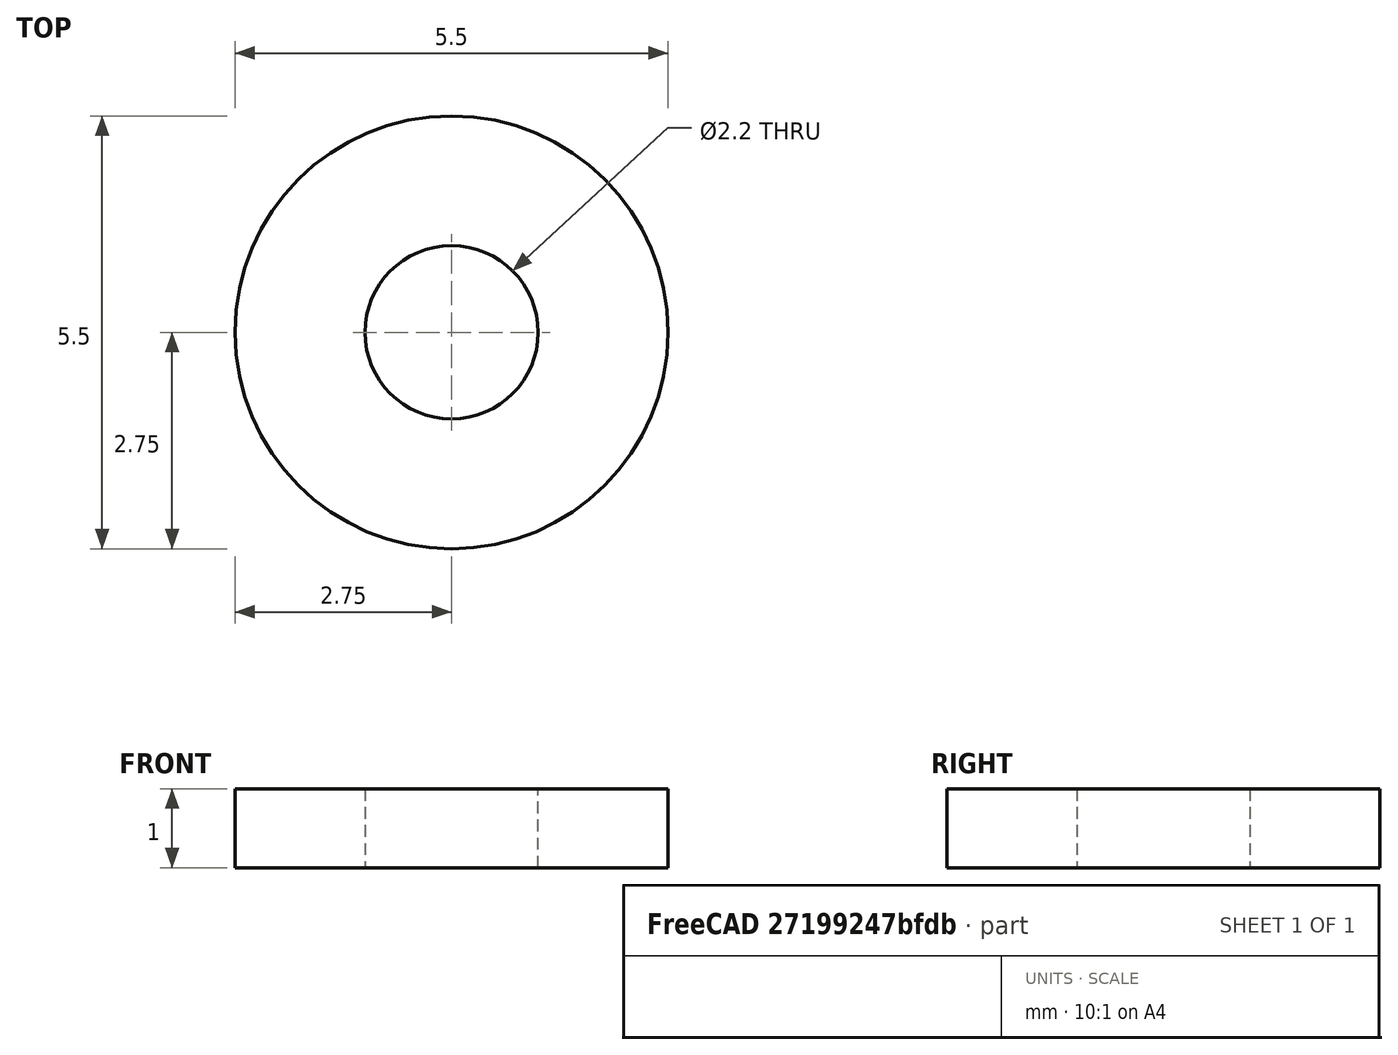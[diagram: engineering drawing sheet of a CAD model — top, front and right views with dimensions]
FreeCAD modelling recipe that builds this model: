
FCSTD DOCUMENT  (FreeCAD 0.18R13959 (Git))
Label: Washer_M2x1mm
License: CreativeCommons Attribution-NonCommercial-ShareAlike
LicenseURL: http://creativecommons.org/licenses/by-nc-sa/4.0/
objects: Sketcher::SketchObject×1, PartDesign::Pad×1, PartDesign::Body×1, Mesh::Feature×1
note: 4 computed .brp shape members not serialized (recipe doc carries the construction recipe); baked Part::Feature solids carry a one-line shape summary decoded from their .brp

FEATURE [Sketcher::SketchObject] Sketch
  MapMode = 5
  Support = -> [XY_Plane]
  sketch-geometry (2):
    g0: Circle CenterX=0 CenterY=0 CenterZ=0 NormalX=0 NormalY=0 NormalZ=1 AngleXU=0 Radius=2.75
    g1: Circle CenterX=0 CenterY=0 CenterZ=0 NormalX=0 NormalY=0 NormalZ=1 AngleXU=0 Radius=1.1
  constraints (4):
    c: Coincident(g0,g-1)
    c: Radius(g0) = 2.75
    c: Coincident(g1,g-1)
    c: Radius(g1) = 1.1
FEATURE [PartDesign::Pad] Pad
  Length = 1
  Length2 = 100
  Profile = -> Sketch
  Type = 0
FEATURE [PartDesign::Body] Body
  Group = -> [Sketch,Pad]
  Origin = -> Origin
  Tip = -> Pad
FEATURE [Mesh::Feature] Mesh  label="Pad (Meshed)"
